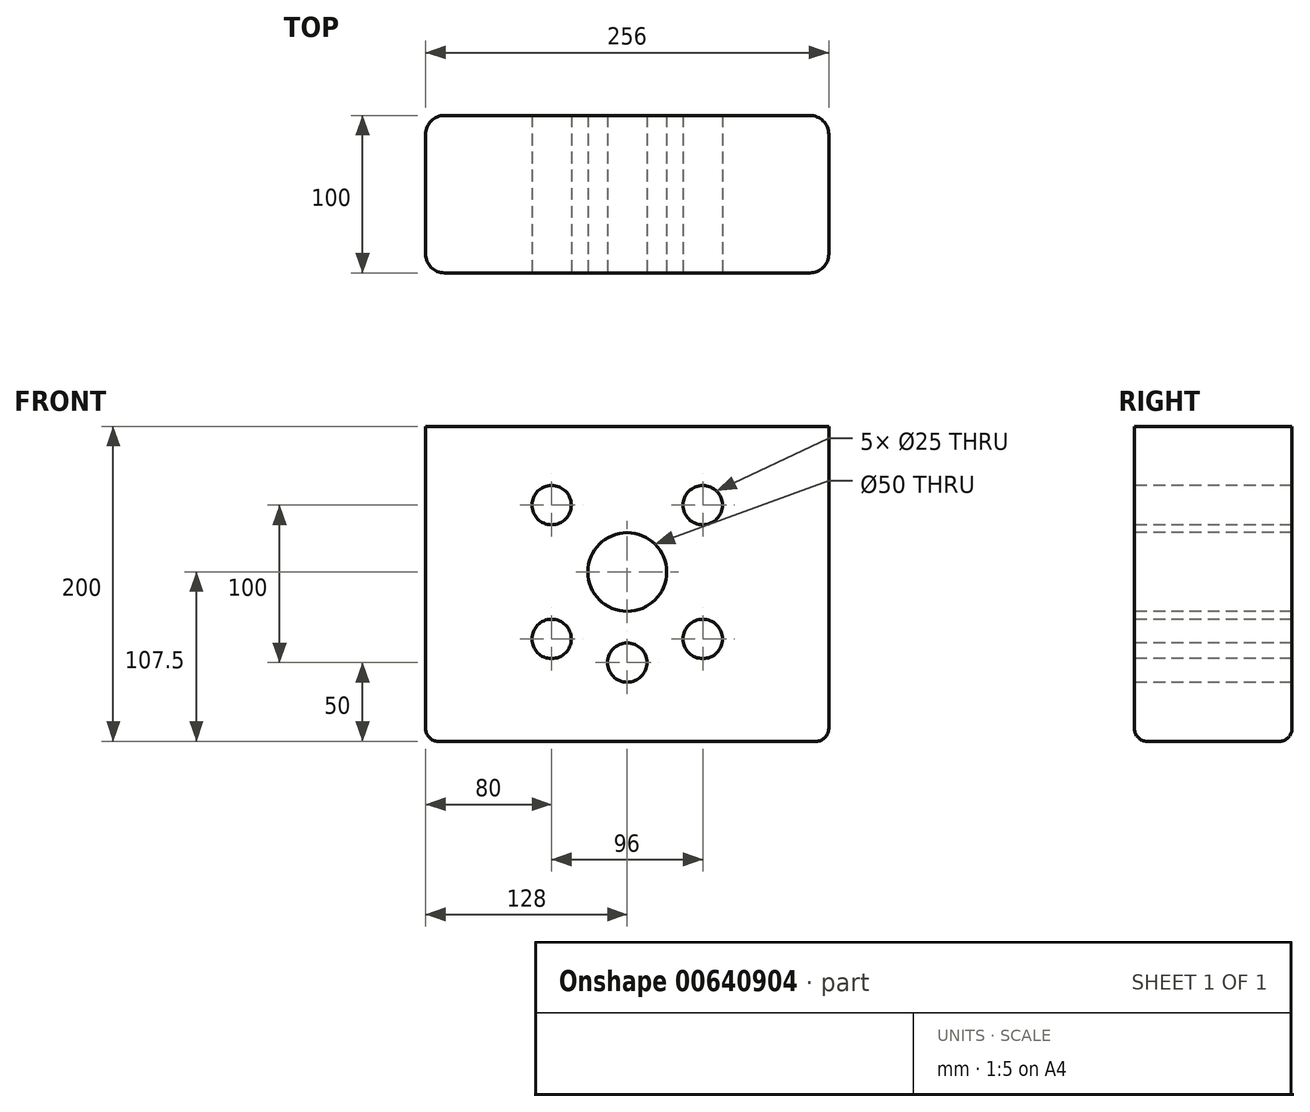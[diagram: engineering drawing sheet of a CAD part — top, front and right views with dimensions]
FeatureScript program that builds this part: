
annotation { "Feature Type Name" : "Feature", "Feature Type Description" : "" }
export const myFeature = defineFeature(function(context is Context, id is Id, definition is map)
    precondition{}
    {
        {
            var Q0;
            Q0=qCreatedBy(makeId("Top.planeOp"),FACE);
            var sketch = newSketch(context, id + "F0", { "sketchPlane" : qUnion([Q0])});
            skLineSegment(sketch, "E0.bottom", {"start": v(-116, 50) * mm, "end": v(116, 50) * mm});
            skLineSegment(sketch, "E0.top", {"start": v(-116, -50) * mm, "end": v(116, -50) * mm});
            skLineSegment(sketch, "E0.left", {"start": v(-128, 38) * mm, "end": v(-128, -38) * mm});
            skLineSegment(sketch, "E0.right", {"start": v(128, 38) * mm, "end": v(128, -38) * mm});
            skPoint(sketch, "E1.visualSharp", {"position": v(-128, 50) * mm});
            skArc(sketch, "E1.filletArc", {"start": v(-116, 50) * mm, "mid": v(-124.49, 46.49) * mm, "end": v(-128, 38) * mm});
            skPoint(sketch, "E2.visualSharp", {"position": v(-128, -50) * mm});
            skArc(sketch, "E2.filletArc", {"start": v(-128, -38) * mm, "mid": v(-124.49, -46.49) * mm, "end": v(-116, -50) * mm});
            skPoint(sketch, "E3.visualSharp", {"position": v(128, -50) * mm});
            skArc(sketch, "E3.filletArc", {"start": v(116, -50) * mm, "mid": v(124.49, -46.49) * mm, "end": v(128, -38) * mm});
            skPoint(sketch, "E4.visualSharp", {"position": v(128, 50) * mm});
            skArc(sketch, "E4.filletArc", {"start": v(128, 38) * mm, "mid": v(124.49, 46.49) * mm, "end": v(116, 50) * mm});
            skSolve(sketch);
        }
        {
            var Q0;
            Q0=makeQuery(id+"F0.imprint","IMPRINT",FACE,{"disambiguationData":[TD([[makeQuery(id+"F0.imprint","IMPRINT",EDGE,{"derivedFrom":sQuery(id+"F0.wireOp",EDGE,"E0.bottom")}),-1.0]])]});
            extrude(context, id + "F1", {"entities" : qUnion([Q0]), "oppositeDirection" : true, "depth" : 200 * mm, "offsetDistance" : 25 * mm});
        }
        {
            var Q0;
            Q0=makeQuery(id+"F1.opExtrude","SWEPT_FACE",FACE,{"disambiguationData":[OSD([sQuery(id+"F0.wireOp",EDGE,"E0.top")])]});
            var sketch = newSketch(context, id + "F2", { "sketchPlane" : qUnion([Q0])});
            skPoint(sketch, "E5", {"position": v(-48, -50) * mm});
            skPoint(sketch, "E6", {"position": v(48, -50) * mm});
            skPoint(sketch, "E7", {"position": v(48, -135) * mm});
            skPoint(sketch, "E8", {"position": v(0, -150) * mm});
            skPoint(sketch, "E9", {"position": v(-48, -135) * mm});
            skLineSegment(sketch, "E10", {"start": v(-48, -50) * mm, "end": v(48, -135) * mm});
            skLineSegment(sketch, "E11", {"start": v(48, -50) * mm, "end": v(-48, -135) * mm});
            skPoint(sketch, "E12", {"position": v(0, -92.5) * mm});
            skSolve(sketch);
        }
        {
            var Q0;
            Q0=sQuery(id+"F2.wireOp",VERTEX,"E5");
            var Q1;
            Q1=sQuery(id+"F2.wireOp",VERTEX,"E6");
            var Q2;
            Q2=sQuery(id+"F2.wireOp",VERTEX,"E7");
            var Q3;
            Q3=sQuery(id+"F2.wireOp",VERTEX,"E8");
            var Q4;
            Q4=sQuery(id+"F2.wireOp",VERTEX,"E9");
            var Q5;
            Q5=makeQuery(id+"F1.opExtrude","SWEPT_BODY",BODY,{"disambiguationData":[OSD([sQuery(id+"F0.wireOp",EDGE,"E0.bottom"),sQuery(id+"F0.wireOp",EDGE,"E0.top"),sQuery(id+"F0.wireOp",EDGE,"E0.left"),sQuery(id+"F0.wireOp",EDGE,"E0.right"),sQuery(id+"F0.wireOp",EDGE,"E1.filletArc"),sQuery(id+"F0.wireOp",EDGE,"E2.filletArc"),sQuery(id+"F0.wireOp",EDGE,"E3.filletArc"),sQuery(id+"F0.wireOp",EDGE,"E4.filletArc")])]});
            hole(context, id + "F3", {"style" : HoleStyle.SIMPLE, "endStyle" : HoleEndStyle.THROUGH, "holeDiameter" : 25 * mm, "majorDiameter" : 5 * mm, "isTappedThrough" : true, "tappedDepth" : 12 * mm, "tapClearance" : 3, "locations" : qUnion([Q0, Q1, Q2, Q3, Q4]), "scope" : qUnion([Q5])});
        }
        {
            var Q0;
            Q0=makeQuery(id+"F1.opExtrude","CAP_EDGE",EDGE,{"disambiguationData":[OSD([sQuery(id+"F0.wireOp",EDGE,"E0.right")])],"isStart":false});
            fillet(context, id + "F4", {"entities" : qUnion([Q0]), "radius" : 8 * mm, "tangentPropagation" : true, "allowEdgeOverflow" : false});
        }
        {
            var Q0;
            Q0=sQuery(id+"F2.wireOp",VERTEX,"E12");
            var Q1;
            Q1=makeQuery(id+"F1.opExtrude","SWEPT_BODY",BODY,{"disambiguationData":[OSD([sQuery(id+"F0.wireOp",EDGE,"E0.bottom"),sQuery(id+"F0.wireOp",EDGE,"E0.top"),sQuery(id+"F0.wireOp",EDGE,"E0.left"),sQuery(id+"F0.wireOp",EDGE,"E0.right"),sQuery(id+"F0.wireOp",EDGE,"E1.filletArc"),sQuery(id+"F0.wireOp",EDGE,"E2.filletArc"),sQuery(id+"F0.wireOp",EDGE,"E3.filletArc"),sQuery(id+"F0.wireOp",EDGE,"E4.filletArc")])]});
            hole(context, id + "F5", {"style" : HoleStyle.SIMPLE, "endStyle" : HoleEndStyle.THROUGH, "holeDiameter" : 50 * mm, "majorDiameter" : 5 * mm, "isTappedThrough" : true, "tappedDepth" : 12 * mm, "tapClearance" : 3, "locations" : qUnion([Q0]), "scope" : qUnion([Q1])});
        }
    });
